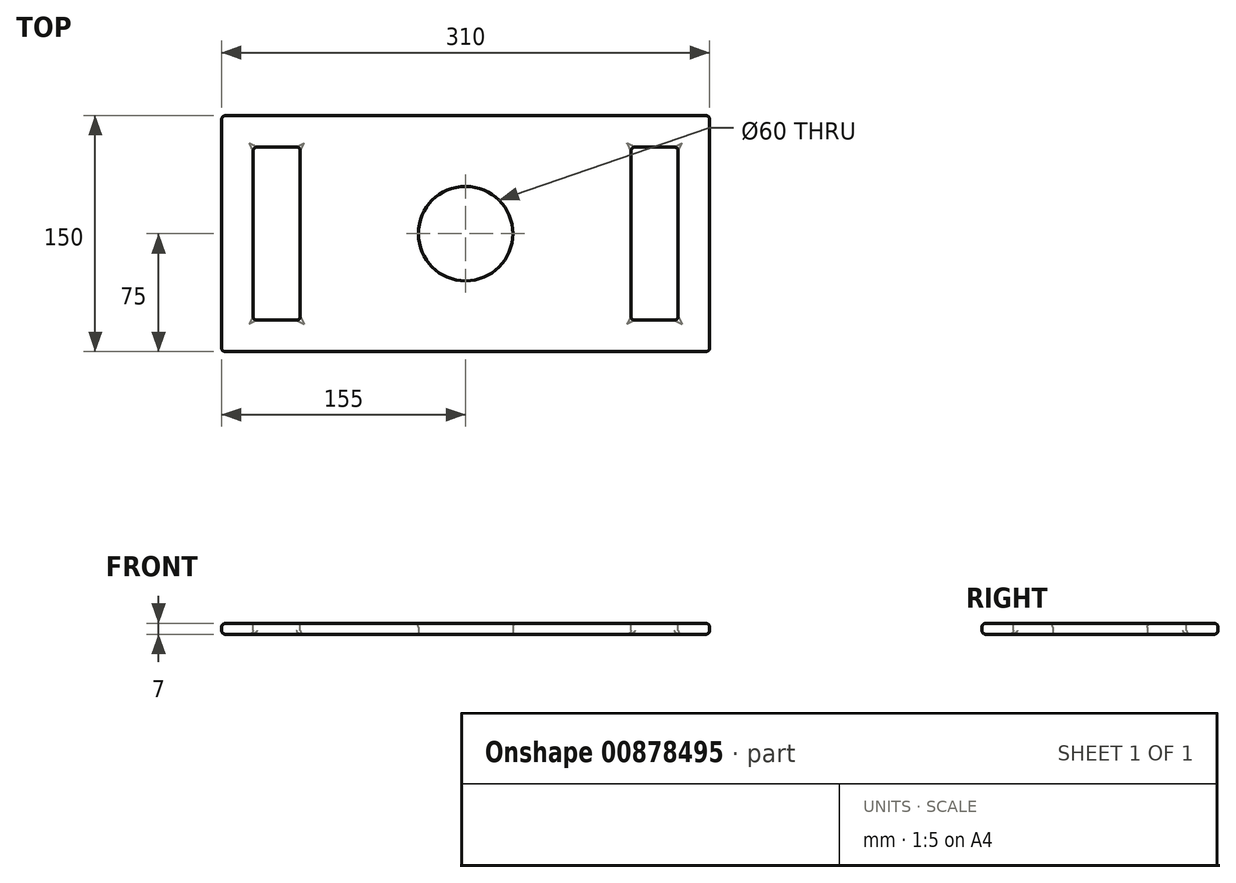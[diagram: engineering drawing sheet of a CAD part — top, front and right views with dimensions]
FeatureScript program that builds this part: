
annotation { "Feature Type Name" : "Feature", "Feature Type Description" : "" }
export const myFeature = defineFeature(function(context is Context, id is Id, definition is map)
    precondition{}
    {
        {
            var Q0;
            Q0=qCreatedBy(makeId("Top.planeOp"),FACE);
            var sketch = newSketch(context, id + "F0", { "sketchPlane" : qUnion([Q0])});
            skLineSegment(sketch, "E0.bottom", {"start": v(0, 0) * mm, "end": v(-310, 0) * mm});
            skLineSegment(sketch, "E0.top", {"start": v(0, 150) * mm, "end": v(-310, 150) * mm});
            skLineSegment(sketch, "E0.left", {"start": v(0, 0) * mm, "end": v(0, 150) * mm});
            skLineSegment(sketch, "E0.right", {"start": v(-310, 0) * mm, "end": v(-310, 150) * mm});
            skSolve(sketch);
        }
        {
            var Q0;
            Q0=makeQuery(id+"F0.imprint","IMPRINT",FACE,{"disambiguationData":[TD([[makeQuery(id+"F0.imprint","IMPRINT",EDGE,{"derivedFrom":sQuery(id+"F0.wireOp",EDGE,"E0.bottom")}),-1.0]])]});
            extrude(context, id + "F1", {"entities" : qUnion([Q0]), "depth" : 7 * mm, "offsetDistance" : 25.4 * mm});
        }
        {
            var Q0;
            Q0=makeQuery(id+"F1.opExtrude","CAP_FACE",FACE,{"disambiguationData":[OSD([sQuery(id+"F0.wireOp",EDGE,"E0.bottom"),sQuery(id+"F0.wireOp",EDGE,"E0.top"),sQuery(id+"F0.wireOp",EDGE,"E0.left"),sQuery(id+"F0.wireOp",EDGE,"E0.right")])],"isStart":true});
            var sketch = newSketch(context, id + "F2", { "sketchPlane" : qUnion([Q0])});
            skCircle(sketch, "E1", {"center": v(-155, -75) * mm, "radius": 30 * mm});
            skSolve(sketch);
        }
        {
            var Q0;
            Q0=makeQuery(id+"F2.imprint","IMPRINT",FACE,{"disambiguationData":[TD([[makeQuery(id+"F2.imprint","IMPRINT",EDGE,{"derivedFrom":sQuery(id+"F2.wireOp",EDGE,"E1")}),1.0]])]});
            extrude(context, id + "F3", {"entities" : qUnion([Q0]), "operationType" : NewBodyOperationType.REMOVE, "endBound" : BoundingType.THROUGH_ALL, "oppositeDirection" : true, "depth" : 25.4 * mm, "offsetDistance" : 25.4 * mm});
        }
        {
            var Q0;
            Q0=makeQuery(id+"F1.opExtrude","CAP_FACE",FACE,{"disambiguationData":[OSD([sQuery(id+"F0.wireOp",EDGE,"E0.bottom"),sQuery(id+"F0.wireOp",EDGE,"E0.top"),sQuery(id+"F0.wireOp",EDGE,"E0.left"),sQuery(id+"F0.wireOp",EDGE,"E0.right")])],"isStart":false});
            var sketch = newSketch(context, id + "F4", { "sketchPlane" : qUnion([Q0])});
            skLineSegment(sketch, "E2.bottom", {"start": v(-290, 130) * mm, "end": v(-260, 130) * mm});
            skLineSegment(sketch, "E2.top", {"start": v(-290, 20) * mm, "end": v(-260, 20) * mm});
            skLineSegment(sketch, "E2.left", {"start": v(-290, 130) * mm, "end": v(-290, 20) * mm});
            skLineSegment(sketch, "E2.right", {"start": v(-260, 130) * mm, "end": v(-260, 20) * mm});
            skLineSegment(sketch, "E3.bottom", {"start": v(-50, 130) * mm, "end": v(-20, 130) * mm});
            skLineSegment(sketch, "E3.top", {"start": v(-50, 20) * mm, "end": v(-20, 20) * mm});
            skLineSegment(sketch, "E3.left", {"start": v(-50, 130) * mm, "end": v(-50, 20) * mm});
            skLineSegment(sketch, "E3.right", {"start": v(-20, 130) * mm, "end": v(-20, 20) * mm});
            skSolve(sketch);
        }
        {
            var Q0;
            Q0=makeQuery(id+"F4.imprint","IMPRINT",FACE,{"disambiguationData":[TD([[makeQuery(id+"F4.imprint","IMPRINT",EDGE,{"derivedFrom":sQuery(id+"F4.wireOp",EDGE,"E2.bottom")}),-1.0]])]});
            var Q1;
            Q1=makeQuery(id+"F4.imprint","IMPRINT",FACE,{"disambiguationData":[TD([[makeQuery(id+"F4.imprint","IMPRINT",EDGE,{"derivedFrom":sQuery(id+"F4.wireOp",EDGE,"E3.bottom")}),-1.0]])]});
            extrude(context, id + "F5", {"entities" : qUnion([Q0, Q1]), "operationType" : NewBodyOperationType.REMOVE, "endBound" : BoundingType.THROUGH_ALL, "oppositeDirection" : true, "depth" : 25.4 * mm, "offsetDistance" : 25.4 * mm});
        }
        {
            var Q0;
            Q0=makeQuery(id+"F1.opExtrude","CAP_EDGE",EDGE,{"disambiguationData":[OSD([sQuery(id+"F0.wireOp",EDGE,"E0.right")])],"isStart":false});
            var Q1;
            Q1=makeQuery(id+"F1.opExtrude","CAP_EDGE",EDGE,{"disambiguationData":[OSD([sQuery(id+"F0.wireOp",EDGE,"E0.top")])],"isStart":false});
            var Q2;
            Q2=makeQuery(id+"F1.opExtrude","CAP_EDGE",EDGE,{"disambiguationData":[OSD([sQuery(id+"F0.wireOp",EDGE,"E0.left")])],"isStart":false});
            var Q3;
            Q3=makeQuery(id+"F1.opExtrude","CAP_EDGE",EDGE,{"disambiguationData":[OSD([sQuery(id+"F0.wireOp",EDGE,"E0.bottom")])],"isStart":false});
            var Q4;
            Q4=makeQuery(id+"F3.boolean.opBoolean","INTERSECT",EDGE,{"derivedFrom":[makeQuery(id+"F1.opExtrude","CAP_FACE",FACE,{"disambiguationData":[OSD([sQuery(id+"F0.wireOp",EDGE,"E0.bottom"),sQuery(id+"F0.wireOp",EDGE,"E0.top"),sQuery(id+"F0.wireOp",EDGE,"E0.left"),sQuery(id+"F0.wireOp",EDGE,"E0.right")])],"isStart":false}),makeQuery(id+"F3.opExtrude","SWEPT_FACE",FACE,{"disambiguationData":[OSD([sQuery(id+"F2.wireOp",EDGE,"E1")])]})]});
            var Q5;
            Q5=makeQuery(id+"F5.boolean.opBoolean","COPY",EDGE,{"derivedFrom":makeQuery(id+"F5.opExtrude","CAP_EDGE",EDGE,{"disambiguationData":[OSD([sQuery(id+"F4.wireOp",EDGE,"E2.top")])],"isStart":true})});
            var Q6;
            Q6=makeQuery(id+"F5.boolean.opBoolean","COPY",EDGE,{"derivedFrom":makeQuery(id+"F5.opExtrude","CAP_EDGE",EDGE,{"disambiguationData":[OSD([sQuery(id+"F4.wireOp",EDGE,"E2.right")])],"isStart":true})});
            var Q7;
            Q7=makeQuery(id+"F5.boolean.opBoolean","COPY",EDGE,{"derivedFrom":makeQuery(id+"F5.opExtrude","CAP_EDGE",EDGE,{"disambiguationData":[OSD([sQuery(id+"F4.wireOp",EDGE,"E2.left")])],"isStart":true})});
            var Q8;
            Q8=makeQuery(id+"F5.boolean.opBoolean","COPY",EDGE,{"derivedFrom":makeQuery(id+"F5.opExtrude","CAP_EDGE",EDGE,{"disambiguationData":[OSD([sQuery(id+"F4.wireOp",EDGE,"E2.bottom")])],"isStart":true})});
            var Q9;
            Q9=makeQuery(id+"F5.boolean.opBoolean","COPY",EDGE,{"derivedFrom":makeQuery(id+"F5.opExtrude","CAP_EDGE",EDGE,{"disambiguationData":[OSD([sQuery(id+"F4.wireOp",EDGE,"E3.bottom")])],"isStart":true})});
            var Q10;
            Q10=makeQuery(id+"F5.boolean.opBoolean","COPY",EDGE,{"derivedFrom":makeQuery(id+"F5.opExtrude","CAP_EDGE",EDGE,{"disambiguationData":[OSD([sQuery(id+"F4.wireOp",EDGE,"E3.left")])],"isStart":true})});
            var Q11;
            Q11=makeQuery(id+"F5.boolean.opBoolean","COPY",EDGE,{"derivedFrom":makeQuery(id+"F5.opExtrude","CAP_EDGE",EDGE,{"disambiguationData":[OSD([sQuery(id+"F4.wireOp",EDGE,"E3.right")])],"isStart":true})});
            var Q12;
            Q12=makeQuery(id+"F5.boolean.opBoolean","COPY",EDGE,{"derivedFrom":makeQuery(id+"F5.opExtrude","CAP_EDGE",EDGE,{"disambiguationData":[OSD([sQuery(id+"F4.wireOp",EDGE,"E3.top")])],"isStart":true})});
            var Q13;
            Q13=makeQuery(id+"F3.boolean.opBoolean","COPY",EDGE,{"derivedFrom":makeQuery(id+"F3.opExtrude","CAP_EDGE",EDGE,{"disambiguationData":[OSD([sQuery(id+"F2.wireOp",EDGE,"E1")])],"isStart":true})});
            var Q14;
            Q14=makeQuery(id+"F5.boolean.opBoolean","INTERSECT",EDGE,{"derivedFrom":[makeQuery(id+"F1.opExtrude","CAP_FACE",FACE,{"disambiguationData":[OSD([sQuery(id+"F0.wireOp",EDGE,"E0.bottom"),sQuery(id+"F0.wireOp",EDGE,"E0.top"),sQuery(id+"F0.wireOp",EDGE,"E0.left"),sQuery(id+"F0.wireOp",EDGE,"E0.right")])],"isStart":true}),makeQuery(id+"F5.opExtrude","SWEPT_FACE",FACE,{"disambiguationData":[OSD([sQuery(id+"F4.wireOp",EDGE,"E3.left")])]})]});
            var Q15;
            Q15=makeQuery(id+"F5.boolean.opBoolean","INTERSECT",EDGE,{"derivedFrom":[makeQuery(id+"F1.opExtrude","CAP_FACE",FACE,{"disambiguationData":[OSD([sQuery(id+"F0.wireOp",EDGE,"E0.bottom"),sQuery(id+"F0.wireOp",EDGE,"E0.top"),sQuery(id+"F0.wireOp",EDGE,"E0.left"),sQuery(id+"F0.wireOp",EDGE,"E0.right")])],"isStart":true}),makeQuery(id+"F5.opExtrude","SWEPT_FACE",FACE,{"disambiguationData":[OSD([sQuery(id+"F4.wireOp",EDGE,"E3.top")])]})]});
            var Q16;
            Q16=makeQuery(id+"F5.boolean.opBoolean","INTERSECT",EDGE,{"derivedFrom":[makeQuery(id+"F1.opExtrude","CAP_FACE",FACE,{"disambiguationData":[OSD([sQuery(id+"F0.wireOp",EDGE,"E0.bottom"),sQuery(id+"F0.wireOp",EDGE,"E0.top"),sQuery(id+"F0.wireOp",EDGE,"E0.left"),sQuery(id+"F0.wireOp",EDGE,"E0.right")])],"isStart":true}),makeQuery(id+"F5.opExtrude","SWEPT_FACE",FACE,{"disambiguationData":[OSD([sQuery(id+"F4.wireOp",EDGE,"E3.right")])]})]});
            var Q17;
            Q17=makeQuery(id+"F5.boolean.opBoolean","INTERSECT",EDGE,{"derivedFrom":[makeQuery(id+"F1.opExtrude","CAP_FACE",FACE,{"disambiguationData":[OSD([sQuery(id+"F0.wireOp",EDGE,"E0.bottom"),sQuery(id+"F0.wireOp",EDGE,"E0.top"),sQuery(id+"F0.wireOp",EDGE,"E0.left"),sQuery(id+"F0.wireOp",EDGE,"E0.right")])],"isStart":true}),makeQuery(id+"F5.opExtrude","SWEPT_FACE",FACE,{"disambiguationData":[OSD([sQuery(id+"F4.wireOp",EDGE,"E3.bottom")])]})]});
            var Q18;
            Q18=makeQuery(id+"F5.boolean.opBoolean","INTERSECT",EDGE,{"derivedFrom":[makeQuery(id+"F1.opExtrude","CAP_FACE",FACE,{"disambiguationData":[OSD([sQuery(id+"F0.wireOp",EDGE,"E0.bottom"),sQuery(id+"F0.wireOp",EDGE,"E0.top"),sQuery(id+"F0.wireOp",EDGE,"E0.left"),sQuery(id+"F0.wireOp",EDGE,"E0.right")])],"isStart":true}),makeQuery(id+"F5.opExtrude","SWEPT_FACE",FACE,{"disambiguationData":[OSD([sQuery(id+"F4.wireOp",EDGE,"E2.right")])]})]});
            var Q19;
            Q19=makeQuery(id+"F5.boolean.opBoolean","INTERSECT",EDGE,{"derivedFrom":[makeQuery(id+"F1.opExtrude","CAP_FACE",FACE,{"disambiguationData":[OSD([sQuery(id+"F0.wireOp",EDGE,"E0.bottom"),sQuery(id+"F0.wireOp",EDGE,"E0.top"),sQuery(id+"F0.wireOp",EDGE,"E0.left"),sQuery(id+"F0.wireOp",EDGE,"E0.right")])],"isStart":true}),makeQuery(id+"F5.opExtrude","SWEPT_FACE",FACE,{"disambiguationData":[OSD([sQuery(id+"F4.wireOp",EDGE,"E2.bottom")])]})]});
            var Q20;
            Q20=makeQuery(id+"F5.boolean.opBoolean","INTERSECT",EDGE,{"derivedFrom":[makeQuery(id+"F1.opExtrude","CAP_FACE",FACE,{"disambiguationData":[OSD([sQuery(id+"F0.wireOp",EDGE,"E0.bottom"),sQuery(id+"F0.wireOp",EDGE,"E0.top"),sQuery(id+"F0.wireOp",EDGE,"E0.left"),sQuery(id+"F0.wireOp",EDGE,"E0.right")])],"isStart":true}),makeQuery(id+"F5.opExtrude","SWEPT_FACE",FACE,{"disambiguationData":[OSD([sQuery(id+"F4.wireOp",EDGE,"E2.left")])]})]});
            var Q21;
            Q21=makeQuery(id+"F5.boolean.opBoolean","INTERSECT",EDGE,{"derivedFrom":[makeQuery(id+"F1.opExtrude","CAP_FACE",FACE,{"disambiguationData":[OSD([sQuery(id+"F0.wireOp",EDGE,"E0.bottom"),sQuery(id+"F0.wireOp",EDGE,"E0.top"),sQuery(id+"F0.wireOp",EDGE,"E0.left"),sQuery(id+"F0.wireOp",EDGE,"E0.right")])],"isStart":true}),makeQuery(id+"F5.opExtrude","SWEPT_FACE",FACE,{"disambiguationData":[OSD([sQuery(id+"F4.wireOp",EDGE,"E2.top")])]})]});
            var Q22;
            Q22=makeQuery(id+"F1.opExtrude","SWEPT_EDGE",EDGE,{"disambiguationData":[OSD([sQuery(id+"F0.wireOp",EDGE,"E0.top"),sQuery(id+"F0.wireOp",EDGE,"E0.left")])]});
            var Q23;
            Q23=makeQuery(id+"F1.opExtrude","SWEPT_EDGE",EDGE,{"disambiguationData":[OSD([sQuery(id+"F0.wireOp",EDGE,"E0.bottom"),sQuery(id+"F0.wireOp",EDGE,"E0.left")])]});
            var Q24;
            Q24=makeQuery(id+"F1.opExtrude","CAP_EDGE",EDGE,{"disambiguationData":[OSD([sQuery(id+"F0.wireOp",EDGE,"E0.left")])],"isStart":true});
            var Q25;
            Q25=makeQuery(id+"F1.opExtrude","CAP_EDGE",EDGE,{"disambiguationData":[OSD([sQuery(id+"F0.wireOp",EDGE,"E0.bottom")])],"isStart":true});
            var Q26;
            Q26=makeQuery(id+"F1.opExtrude","CAP_EDGE",EDGE,{"disambiguationData":[OSD([sQuery(id+"F0.wireOp",EDGE,"E0.top")])],"isStart":true});
            var Q27;
            Q27=makeQuery(id+"F1.opExtrude","CAP_EDGE",EDGE,{"disambiguationData":[OSD([sQuery(id+"F0.wireOp",EDGE,"E0.right")])],"isStart":true});
            fillet(context, id + "F6", {"entities" : qUnion([Q0, Q1, Q2, Q3, Q4, Q5, Q6, Q7, Q8, Q9, Q10, Q11, Q12, Q13, Q14, Q15, Q16, Q17, Q18, Q19, Q20, Q21, Q22, Q23, Q24, Q25, Q26, Q27]), "radius" : 2.54 * mm, "tangentPropagation" : true, "allowEdgeOverflow" : false});
        }
        {
            var Q0;
            Q0=makeQuery(id+"F1.opExtrude","SWEPT_EDGE",EDGE,{"disambiguationData":[OSD([sQuery(id+"F0.wireOp",EDGE,"E0.bottom"),sQuery(id+"F0.wireOp",EDGE,"E0.right")])]});
            var Q1;
            Q1=makeQuery(id+"F1.opExtrude","SWEPT_EDGE",EDGE,{"disambiguationData":[OSD([sQuery(id+"F0.wireOp",EDGE,"E0.top"),sQuery(id+"F0.wireOp",EDGE,"E0.right")])]});
            var Q2;
            Q2=makeQuery(id+"F5.boolean.opBoolean","COPY",EDGE,{"derivedFrom":makeQuery(id+"F5.opExtrude","SWEPT_EDGE",EDGE,{"disambiguationData":[OSD([sQuery(id+"F4.wireOp",EDGE,"E2.bottom"),sQuery(id+"F4.wireOp",EDGE,"E2.right")])]})});
            var Q3;
            Q3=makeQuery(id+"F5.boolean.opBoolean","COPY",EDGE,{"derivedFrom":makeQuery(id+"F5.opExtrude","SWEPT_EDGE",EDGE,{"disambiguationData":[OSD([sQuery(id+"F4.wireOp",EDGE,"E3.bottom"),sQuery(id+"F4.wireOp",EDGE,"E3.right")])]})});
            var Q4;
            Q4=makeQuery(id+"F5.boolean.opBoolean","COPY",EDGE,{"derivedFrom":makeQuery(id+"F5.opExtrude","SWEPT_EDGE",EDGE,{"disambiguationData":[OSD([sQuery(id+"F4.wireOp",EDGE,"E3.top"),sQuery(id+"F4.wireOp",EDGE,"E3.right")])]})});
            var Q5;
            Q5=makeQuery(id+"F5.boolean.opBoolean","COPY",EDGE,{"derivedFrom":makeQuery(id+"F5.opExtrude","SWEPT_EDGE",EDGE,{"disambiguationData":[OSD([sQuery(id+"F4.wireOp",EDGE,"E2.top"),sQuery(id+"F4.wireOp",EDGE,"E2.right")])]})});
            var Q6;
            Q6=makeQuery(id+"F5.boolean.opBoolean","COPY",EDGE,{"derivedFrom":makeQuery(id+"F5.opExtrude","SWEPT_EDGE",EDGE,{"disambiguationData":[OSD([sQuery(id+"F4.wireOp",EDGE,"E2.top"),sQuery(id+"F4.wireOp",EDGE,"E2.left")])]})});
            var Q7;
            Q7=makeQuery(id+"F5.boolean.opBoolean","COPY",EDGE,{"derivedFrom":makeQuery(id+"F5.opExtrude","SWEPT_EDGE",EDGE,{"disambiguationData":[OSD([sQuery(id+"F4.wireOp",EDGE,"E3.top"),sQuery(id+"F4.wireOp",EDGE,"E3.left")])]})});
            var Q8;
            Q8=makeQuery(id+"F5.boolean.opBoolean","COPY",EDGE,{"derivedFrom":makeQuery(id+"F5.opExtrude","SWEPT_EDGE",EDGE,{"disambiguationData":[OSD([sQuery(id+"F4.wireOp",EDGE,"E2.bottom"),sQuery(id+"F4.wireOp",EDGE,"E2.left")])]})});
            var Q9;
            Q9=makeQuery(id+"F5.boolean.opBoolean","COPY",EDGE,{"derivedFrom":makeQuery(id+"F5.opExtrude","SWEPT_EDGE",EDGE,{"disambiguationData":[OSD([sQuery(id+"F4.wireOp",EDGE,"E3.bottom"),sQuery(id+"F4.wireOp",EDGE,"E3.left")])]})});
            fillet(context, id + "F7", {"entities" : qUnion([Q0, Q1, Q2, Q3, Q4, Q5, Q6, Q7, Q8, Q9]), "radius" : 2.54 * mm, "tangentPropagation" : true, "allowEdgeOverflow" : false});
        }
    });
